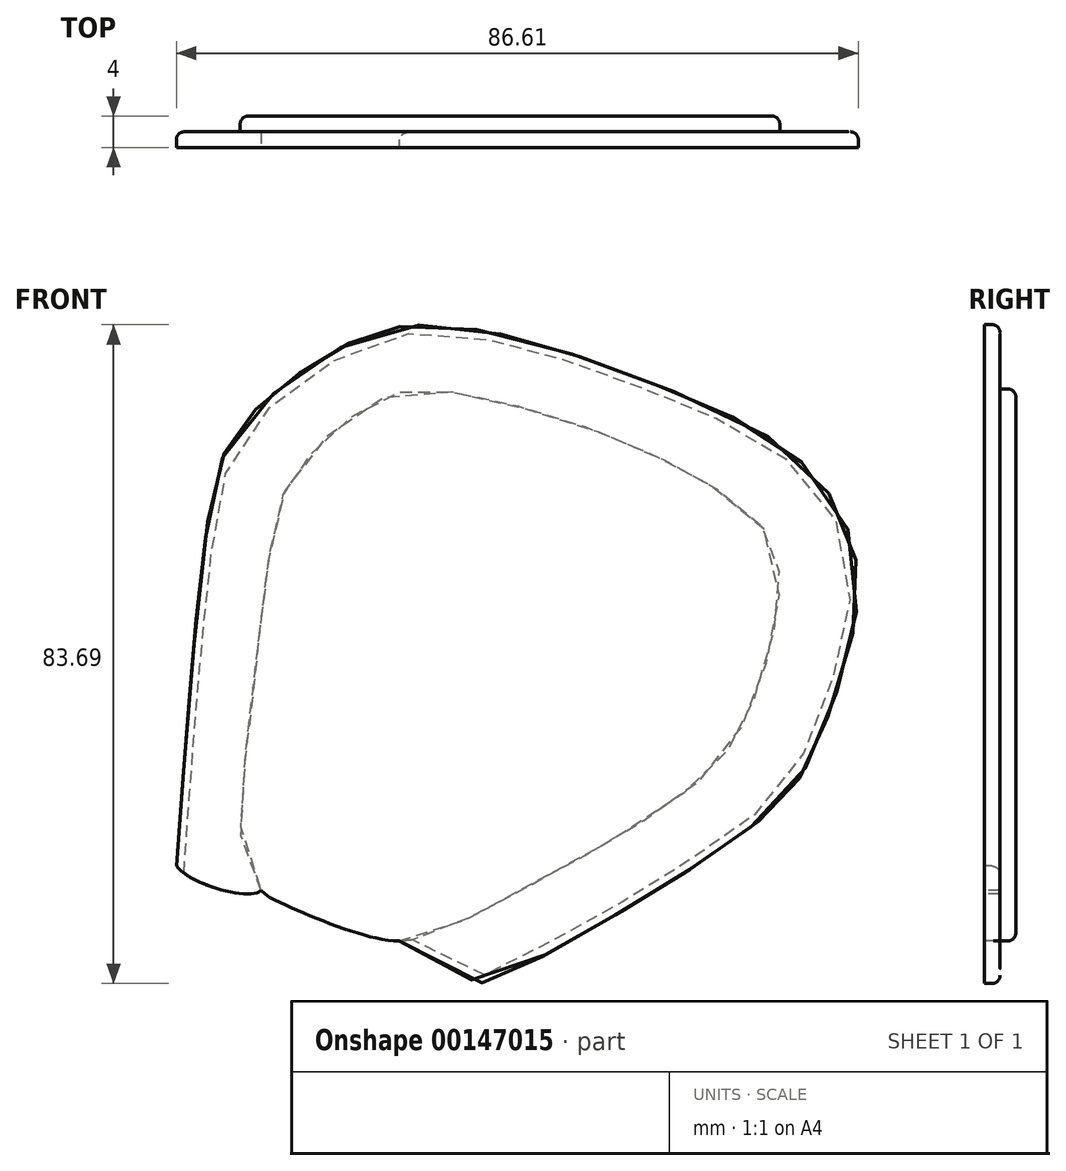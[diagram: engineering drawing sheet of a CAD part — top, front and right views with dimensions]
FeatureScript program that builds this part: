
annotation { "Feature Type Name" : "Feature", "Feature Type Description" : "" }
export const myFeature = defineFeature(function(context is Context, id is Id, definition is map)
    precondition{}
    {
        {
            var Q0;
            Q0=qCreatedBy(makeId("Front.planeOp"),FACE);
            var sketch = newSketch(context, id + "F0", { "sketchPlane" : qUnion([Q0])});
            skFitSpline(sketch, "E0", {"points": [v(-17.37, 64.05) * mm, v(-11.7, 62.91) * mm, v(-4.77, 60.93) * mm, v(2.03, 58.67) * mm, v(7.27, 56.4) * mm, v(12.01, 54.14) * mm, v(15.2, 52.22) * mm, v(18.67, 50.17) * mm, v(21.36, 47.55) * mm, v(22.91, 45) * mm, v(23.7, 42.52) * mm, v(23.98, 39.27) * mm, v(23.48, 35.23) * mm, v(22.18, 29.33) * mm, v(20.48, 24.62) * mm, v(18.98, 21.22) * mm, v(16.77, 17.81) * mm, v(13.97, 14.9) * mm, v(9.86, 11.8) * mm, v(2.15, 6.9) * mm, v(-4.45, 3.3) * mm, v(-11.86, -0.81) * mm, v(-16.77, -3.31) * mm, v(-20.67, -5.02) * mm, v(-24.38, -5.62) * mm, v(-28.28, -5.02) * mm, v(-33.69, -3.21) * mm, v(-38.7, -1.11) * mm, v(-41.9, 0.8) * mm, v(-43.6, 3.9) * mm, v(-44.5, 8.2) * mm, v(-44.2, 15.3) * mm, v(-43.1, 24.42) * mm, v(-41.7, 37.44) * mm, v(-40.4, 45.95) * mm, v(-39.4, 50.05) * mm, v(-38.3, 52.85) * mm, v(-36.4, 55.26) * mm, v(-34.6, 57.36) * mm, v(-31.99, 59.86) * mm, v(-29.18, 61.76) * mm, v(-26.58, 63.27) * mm, v(-23.18, 64.37) * mm, v(-20.37, 64.47) * mm, v(-17.37, 64.05) * mm]});
            skFitSpline(sketch, "E1", {"points": [v(-52.66, 3.9) * mm, v(-51.46, 20.08) * mm, v(-48.77, 47) * mm, v(-46.83, 55.7) * mm, v(-44.8, 59.5) * mm, v(-40.72, 63.57) * mm, v(-36.74, 66.72) * mm, v(-31.75, 69.77) * mm, v(-27.68, 71.53) * mm, v(-22.03, 72.64) * mm, v(-10.1, 71.16) * mm, v(7.03, 65.52) * mm, v(23.4, 57.84) * mm, v(31, 50.06) * mm, v(33.77, 42.2) * mm, v(33.22, 33.22) * mm, v(29.51, 21.47) * mm, v(26.46, 15) * mm, v(23.31, 11.2) * mm, v(14.52, 4.81) * mm, v(5.92, -0.74) * mm, v(-5.84, -7.4) * mm, v(-12.5, -11.01) * mm, v(-24.38, -5.62) * mm], "startDerivative": vector(18.24, 257.74) * mm, "endDerivative": vector(-260.09, 165.04) * mm});
            skFitSpline(sketch, "E2", {"points": [v(-52.66, 3.9) * mm, v(-41.9, 0.8) * mm], "startDerivative": vector(4.72, -6.69) * mm, "endDerivative": vector(4.8, 4.31) * mm});
            skSolve(sketch);
        }
        {
            var Q0;
            {var subQ0=sQuery(id+"F0.wireOp",EDGE,"E1");Q0=makeQuery(id+"F0.imprint","IMPRINT",FACE,{"disambiguationData":[TD([[makeQuery(id+"F0.imprint","IMPRINT",EDGE,{"derivedFrom":subQ0}),-1.0]])]});}
            extrude(context, id + "F1", {"entities" : qUnion([Q0]), "oppositeDirection" : true, "depth" : 2 * mm, "offsetDistance" : 25 * mm});
        }
        {
            var Q0;
            {var subQ0=sQuery(id+"F0.wireOp",EDGE,"E0");var subQ1=makeQuery(id+"F0.imprint","INTERSECT",VERTEX,{"derivedFrom":[subQ0,sQuery(id+"F0.wireOp",EDGE,"E1")]});Q0=makeQuery(id+"F0.imprint","IMPRINT",FACE,{"disambiguationData":[TD([[makeQuery(id+"F0.imprint","IMPRINT",EDGE,{"disambiguationData":[TD([[subQ1,-1.0]])],"derivedFrom":subQ0}),-1.0]])]});}
            extrude(context, id + "F2", {"entities" : qUnion([Q0]), "operationType" : NewBodyOperationType.ADD, "oppositeDirection" : true, "depth" : 4 * mm, "offsetDistance" : 25 * mm});
        }
        {
            var Q0;
            Q0=makeQuery(id+"F2.opExtrude","CAP_EDGE",EDGE,{"disambiguationData":[OSD([sQuery(id+"F0.wireOp",EDGE,"E0")])],"isStart":false});
            var Q1;
            Q1=makeQuery(id+"F1.opExtrude","CAP_EDGE",EDGE,{"disambiguationData":[OSD([sQuery(id+"F0.wireOp",EDGE,"E1")])],"isStart":false});
            fillet(context, id + "F3", {"entities" : qUnion([Q0, Q1]), "radius" : 1 * mm, "tangentPropagation" : true, "allowEdgeOverflow" : false});
        }
    });
